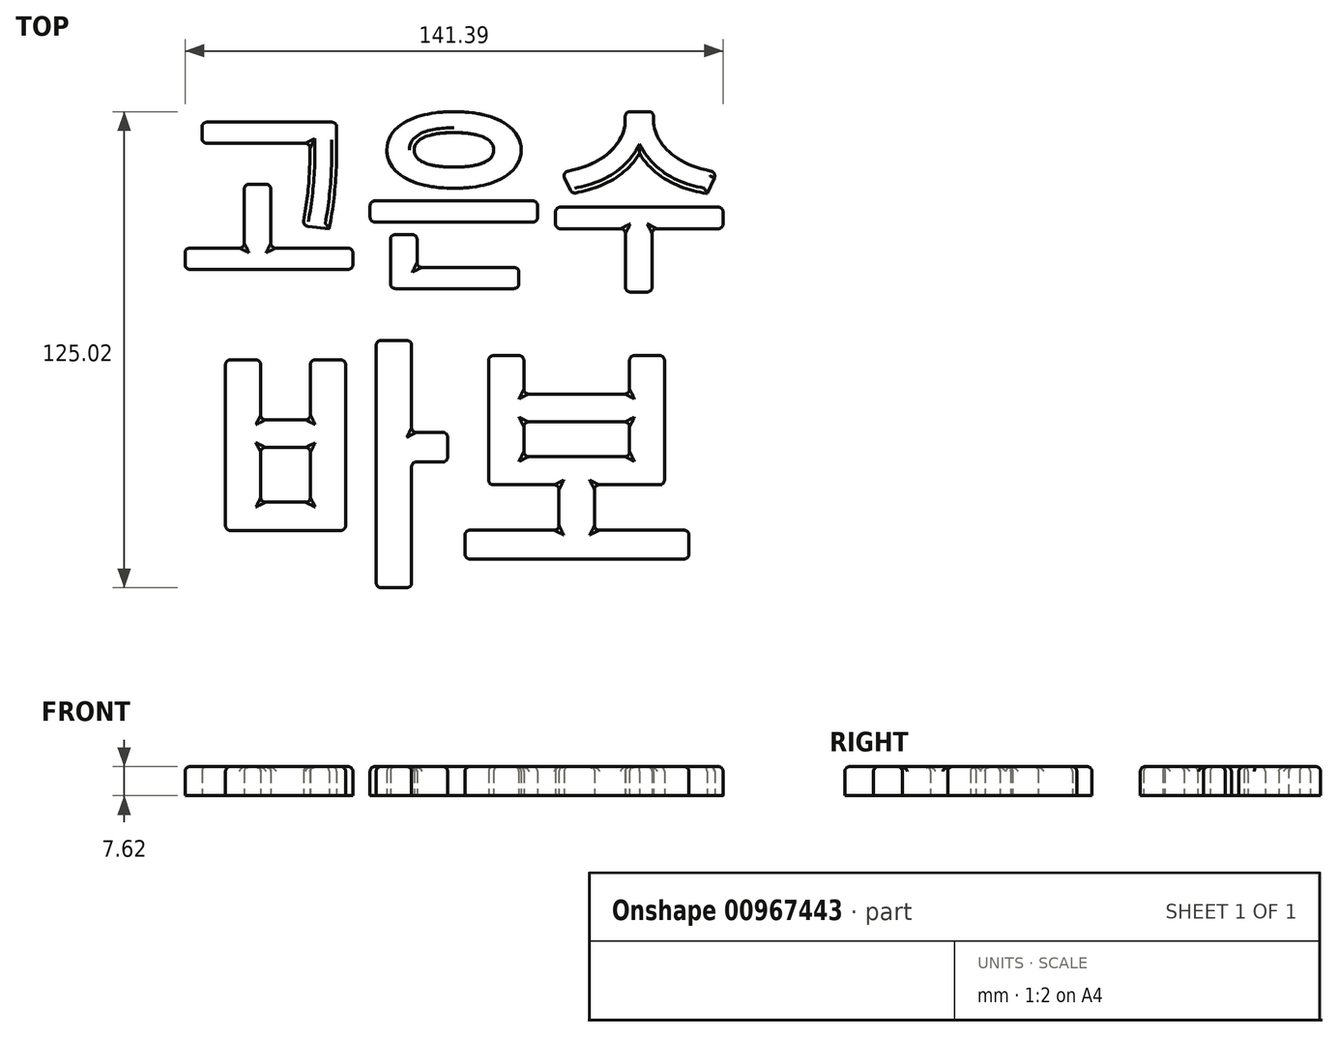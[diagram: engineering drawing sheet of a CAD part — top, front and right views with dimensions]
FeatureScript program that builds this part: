
annotation { "Feature Type Name" : "Feature", "Feature Type Description" : "" }
export const myFeature = defineFeature(function(context is Context, id is Id, definition is map)
    precondition{}
    {
        {
            var Q0;
            Q0=qCreatedBy(makeId("Top.planeOp"),FACE);
            var sketch = newSketch(context, id + "F0", { "sketchPlane" : qUnion([Q0])});
            skText(sketch, "E0", { "text": "고은수", "fontName": "NotoSansCJKkr-Bold.otf"});
            skText(sketch, "E1", { "text": "바보", "fontName": "NotoSansCJKkr-Bold.otf"});
            skLineSegment(sketch, "E2", {"start": v(0, 12.7) * mm, "end": v(0, -12.7) * mm, "construction": true});
            skLineSegment(sketch, "E3", {"start": v(-73.36, 50.8) * mm, "end": v(-73.36, -63.5) * mm, "construction": true});
            const initialGuessF0  = {"E0": [-0.07336, 0.0127, 1, 0, 0.0381], "E1": [-0.0654, -0.0635, 1, 0, 0.0508]};
            skSetInitialGuess(sketch, initialGuessF0);
            skSolve(sketch);
        }
        {
            var Q0;
            Q0 = qSketchRegion(id + "F0", true);
            extrude(context, id + "F1", {"entities" : qUnion([Q0]), "depth" : 7.62 * mm, "offsetDistance" : 25.4 * mm});
        }
        {
            var Q0;
            Q0=makeQuery(id+"F1.opExtrude","CAP_EDGE",EDGE,{"disambiguationData":[OSD([sQuery(id+"F0.wireOp",EDGE,"E0.sketch_text.stroke-4")])],"isStart":false});
            var Q1;
            Q1=makeQuery(id+"F1.opExtrude","CAP_EDGE",EDGE,{"disambiguationData":[OSD([sQuery(id+"F0.wireOp",EDGE,"E0.sketch_text.stroke-3")])],"isStart":false});
            var Q2;
            Q2=makeQuery(id+"F1.opExtrude","CAP_EDGE",EDGE,{"disambiguationData":[OSD([sQuery(id+"F0.wireOp",EDGE,"E0.sketch_text.stroke-2")])],"isStart":false});
            var Q3;
            Q3=makeQuery(id+"F1.opExtrude","CAP_EDGE",EDGE,{"disambiguationData":[OSD([sQuery(id+"F0.wireOp",EDGE,"E0.sketch_text.stroke-0")])],"isStart":false});
            var Q4;
            Q4=makeQuery(id+"F1.opExtrude","CAP_EDGE",EDGE,{"disambiguationData":[OSD([sQuery(id+"F0.wireOp",EDGE,"E0.sketch_text.stroke-5")])],"isStart":false});
            var Q5;
            Q5=makeQuery(id+"F1.opExtrude","CAP_EDGE",EDGE,{"disambiguationData":[OSD([sQuery(id+"F0.wireOp",EDGE,"E0.sketch_text.stroke-6")])],"isStart":false});
            var Q6;
            Q6=makeQuery(id+"F1.opExtrude","CAP_EDGE",EDGE,{"disambiguationData":[OSD([sQuery(id+"F0.wireOp",EDGE,"E0.sketch_text.stroke-7")])],"isStart":false});
            var Q7;
            Q7=makeQuery(id+"F1.opExtrude","CAP_EDGE",EDGE,{"disambiguationData":[OSD([sQuery(id+"F0.wireOp",EDGE,"E0.sketch_text.stroke-8")])],"isStart":false});
            var Q8;
            Q8=makeQuery(id+"F1.opExtrude","CAP_EDGE",EDGE,{"disambiguationData":[OSD([sQuery(id+"F0.wireOp",EDGE,"E0.sketch_text.stroke-10")])],"isStart":false});
            var Q9;
            Q9=makeQuery(id+"F1.opExtrude","CAP_EDGE",EDGE,{"disambiguationData":[OSD([sQuery(id+"F0.wireOp",EDGE,"E0.sketch_text.stroke-11")])],"isStart":false});
            var Q10;
            Q10=makeQuery(id+"F1.opExtrude","CAP_EDGE",EDGE,{"disambiguationData":[OSD([sQuery(id+"F0.wireOp",EDGE,"E0.sketch_text.stroke-12")])],"isStart":false});
            var Q11;
            Q11=makeQuery(id+"F1.opExtrude","CAP_EDGE",EDGE,{"disambiguationData":[OSD([sQuery(id+"F0.wireOp",EDGE,"E0.sketch_text.stroke-14")])],"isStart":false});
            var Q12;
            Q12=makeQuery(id+"F1.opExtrude","CAP_EDGE",EDGE,{"disambiguationData":[OSD([sQuery(id+"F0.wireOp",EDGE,"E0.sketch_text.stroke-13")])],"isStart":false});
            var Q13;
            Q13=makeQuery(id+"F1.opExtrude","CAP_EDGE",EDGE,{"disambiguationData":[OSD([sQuery(id+"F0.wireOp",EDGE,"E0.sketch_text.stroke-29")])],"isStart":false});
            var Q14;
            Q14=makeQuery(id+"F1.opExtrude","CAP_EDGE",EDGE,{"disambiguationData":[OSD([sQuery(id+"F0.wireOp",EDGE,"E0.sketch_text.stroke-32")])],"isStart":false});
            var Q15;
            Q15=makeQuery(id+"F1.opExtrude","CAP_EDGE",EDGE,{"disambiguationData":[OSD([sQuery(id+"F0.wireOp",EDGE,"E0.sketch_text.stroke-9")])],"isStart":false});
            var Q16;
            Q16=makeQuery(id+"F1.opExtrude","CAP_EDGE",EDGE,{"disambiguationData":[OSD([sQuery(id+"F0.wireOp",EDGE,"E0.sketch_text.stroke-30")])],"isStart":false});
            var Q17;
            Q17=makeQuery(id+"F1.opExtrude","CAP_EDGE",EDGE,{"disambiguationData":[OSD([sQuery(id+"F0.wireOp",EDGE,"E0.sketch_text.stroke-31")])],"isStart":false});
            var Q18;
            Q18=makeQuery(id+"F1.opExtrude","CAP_EDGE",EDGE,{"disambiguationData":[OSD([sQuery(id+"F0.wireOp",EDGE,"E0.sketch_text.stroke-19")])],"isStart":false});
            var Q19;
            Q19=makeQuery(id+"F1.opExtrude","CAP_EDGE",EDGE,{"disambiguationData":[OSD([sQuery(id+"F0.wireOp",EDGE,"E0.sketch_text.stroke-16")])],"isStart":false});
            var Q20;
            Q20=makeQuery(id+"F1.opExtrude","CAP_EDGE",EDGE,{"disambiguationData":[OSD([sQuery(id+"F0.wireOp",EDGE,"E0.sketch_text.stroke-27")])],"isStart":false});
            var Q21;
            Q21=makeQuery(id+"F1.opExtrude","CAP_EDGE",EDGE,{"disambiguationData":[OSD([sQuery(id+"F0.wireOp",EDGE,"E0.sketch_text.stroke-28")])],"isStart":false});
            var Q22;
            Q22=makeQuery(id+"F1.opExtrude","CAP_EDGE",EDGE,{"disambiguationData":[OSD([sQuery(id+"F0.wireOp",EDGE,"E0.sketch_text.stroke-23")])],"isStart":false});
            var Q23;
            Q23=makeQuery(id+"F1.opExtrude","CAP_EDGE",EDGE,{"disambiguationData":[OSD([sQuery(id+"F0.wireOp",EDGE,"E0.sketch_text.stroke-24")])],"isStart":false});
            var Q24;
            Q24=makeQuery(id+"F1.opExtrude","CAP_EDGE",EDGE,{"disambiguationData":[OSD([sQuery(id+"F0.wireOp",EDGE,"E0.sketch_text.stroke-25")])],"isStart":false});
            var Q25;
            Q25=makeQuery(id+"F1.opExtrude","CAP_EDGE",EDGE,{"disambiguationData":[OSD([sQuery(id+"F0.wireOp",EDGE,"E0.sketch_text.stroke-26")])],"isStart":false});
            var Q26;
            Q26=makeQuery(id+"F1.opExtrude","CAP_EDGE",EDGE,{"disambiguationData":[OSD([sQuery(id+"F0.wireOp",EDGE,"E0.sketch_text.stroke-43")])],"isStart":false});
            var Q27;
            Q27=makeQuery(id+"F1.opExtrude","CAP_EDGE",EDGE,{"disambiguationData":[OSD([sQuery(id+"F0.wireOp",EDGE,"E0.sketch_text.stroke-44")])],"isStart":false});
            var Q28;
            Q28=makeQuery(id+"F1.opExtrude","CAP_EDGE",EDGE,{"disambiguationData":[OSD([sQuery(id+"F0.wireOp",EDGE,"E0.sketch_text.stroke-45")])],"isStart":false});
            var Q29;
            Q29=makeQuery(id+"F1.opExtrude","CAP_EDGE",EDGE,{"disambiguationData":[OSD([sQuery(id+"F0.wireOp",EDGE,"E0.sketch_text.stroke-47")])],"isStart":false});
            var Q30;
            Q30=makeQuery(id+"F1.opExtrude","CAP_EDGE",EDGE,{"disambiguationData":[OSD([sQuery(id+"F0.wireOp",EDGE,"E0.sketch_text.stroke-48")])],"isStart":false});
            var Q31;
            Q31=makeQuery(id+"F1.opExtrude","CAP_EDGE",EDGE,{"disambiguationData":[OSD([sQuery(id+"F0.wireOp",EDGE,"E0.sketch_text.stroke-42")])],"isStart":false});
            var Q32;
            Q32=makeQuery(id+"F1.opExtrude","CAP_EDGE",EDGE,{"disambiguationData":[OSD([sQuery(id+"F0.wireOp",EDGE,"E0.sketch_text.stroke-46")])],"isStart":false});
            var Q33;
            Q33=makeQuery(id+"F1.opExtrude","CAP_EDGE",EDGE,{"disambiguationData":[OSD([sQuery(id+"F0.wireOp",EDGE,"E0.sketch_text.stroke-40")])],"isStart":false});
            var Q34;
            Q34=makeQuery(id+"F1.opExtrude","CAP_EDGE",EDGE,{"disambiguationData":[OSD([sQuery(id+"F0.wireOp",EDGE,"E0.sketch_text.stroke-39")])],"isStart":false});
            var Q35;
            Q35=makeQuery(id+"F1.opExtrude","CAP_FACE",FACE,{"disambiguationData":[OSD([sQuery(id+"F0.wireOp",EDGE,"E0.sketch_text.stroke-33"),sQuery(id+"F0.wireOp",EDGE,"E0.sketch_text.stroke-34"),sQuery(id+"F0.wireOp",EDGE,"E0.sketch_text.stroke-35"),sQuery(id+"F0.wireOp",EDGE,"E0.sketch_text.stroke-36"),sQuery(id+"F0.wireOp",EDGE,"E0.sketch_text.stroke-37"),sQuery(id+"F0.wireOp",EDGE,"E0.sketch_text.stroke-38"),sQuery(id+"F0.wireOp",EDGE,"E0.sketch_text.stroke-39"),sQuery(id+"F0.wireOp",EDGE,"E0.sketch_text.stroke-40"),sQuery(id+"F0.wireOp",EDGE,"E0.sketch_text.stroke-41")])],"isStart":false});
            var Q36;
            Q36=makeQuery(id+"F1.opExtrude","CAP_EDGE",EDGE,{"disambiguationData":[OSD([sQuery(id+"F0.wireOp",EDGE,"E1.sketch_text.stroke-28")])],"isStart":false});
            var Q37;
            Q37=makeQuery(id+"F1.opExtrude","CAP_EDGE",EDGE,{"disambiguationData":[OSD([sQuery(id+"F0.wireOp",EDGE,"E1.sketch_text.stroke-26")])],"isStart":false});
            var Q38;
            Q38=makeQuery(id+"F1.opExtrude","CAP_FACE",FACE,{"disambiguationData":[OSD([sQuery(id+"F0.wireOp",EDGE,"E1.sketch_text.stroke-20"),sQuery(id+"F0.wireOp",EDGE,"E1.sketch_text.stroke-21"),sQuery(id+"F0.wireOp",EDGE,"E1.sketch_text.stroke-22"),sQuery(id+"F0.wireOp",EDGE,"E1.sketch_text.stroke-23"),sQuery(id+"F0.wireOp",EDGE,"E1.sketch_text.stroke-24"),sQuery(id+"F0.wireOp",EDGE,"E1.sketch_text.stroke-25"),sQuery(id+"F0.wireOp",EDGE,"E1.sketch_text.stroke-26"),sQuery(id+"F0.wireOp",EDGE,"E1.sketch_text.stroke-27"),sQuery(id+"F0.wireOp",EDGE,"E1.sketch_text.stroke-28"),sQuery(id+"F0.wireOp",EDGE,"E1.sketch_text.stroke-29"),sQuery(id+"F0.wireOp",EDGE,"E1.sketch_text.stroke-30"),sQuery(id+"F0.wireOp",EDGE,"E1.sketch_text.stroke-31"),sQuery(id+"F0.wireOp",EDGE,"E1.sketch_text.stroke-32"),sQuery(id+"F0.wireOp",EDGE,"E1.sketch_text.stroke-33"),sQuery(id+"F0.wireOp",EDGE,"E1.sketch_text.stroke-34"),sQuery(id+"F0.wireOp",EDGE,"E1.sketch_text.stroke-35"),sQuery(id+"F0.wireOp",EDGE,"E1.sketch_text.stroke-36"),sQuery(id+"F0.wireOp",EDGE,"E1.sketch_text.stroke-37"),sQuery(id+"F0.wireOp",EDGE,"E1.sketch_text.stroke-38"),sQuery(id+"F0.wireOp",EDGE,"E1.sketch_text.stroke-39")])],"isStart":false});
            var Q39;
            Q39=makeQuery(id+"F1.opExtrude","CAP_FACE",FACE,{"disambiguationData":[OSD([sQuery(id+"F0.wireOp",EDGE,"E1.sketch_text.stroke-12"),sQuery(id+"F0.wireOp",EDGE,"E1.sketch_text.stroke-13"),sQuery(id+"F0.wireOp",EDGE,"E1.sketch_text.stroke-14"),sQuery(id+"F0.wireOp",EDGE,"E1.sketch_text.stroke-15"),sQuery(id+"F0.wireOp",EDGE,"E1.sketch_text.stroke-16"),sQuery(id+"F0.wireOp",EDGE,"E1.sketch_text.stroke-17"),sQuery(id+"F0.wireOp",EDGE,"E1.sketch_text.stroke-18"),sQuery(id+"F0.wireOp",EDGE,"E1.sketch_text.stroke-19")])],"isStart":false});
            var Q40;
            Q40=makeQuery(id+"F1.opExtrude","CAP_FACE",FACE,{"disambiguationData":[OSD([sQuery(id+"F0.wireOp",EDGE,"E1.sketch_text.stroke-0"),sQuery(id+"F0.wireOp",EDGE,"E1.sketch_text.stroke-1"),sQuery(id+"F0.wireOp",EDGE,"E1.sketch_text.stroke-2"),sQuery(id+"F0.wireOp",EDGE,"E1.sketch_text.stroke-3"),sQuery(id+"F0.wireOp",EDGE,"E1.sketch_text.stroke-4"),sQuery(id+"F0.wireOp",EDGE,"E1.sketch_text.stroke-5"),sQuery(id+"F0.wireOp",EDGE,"E1.sketch_text.stroke-6"),sQuery(id+"F0.wireOp",EDGE,"E1.sketch_text.stroke-7"),sQuery(id+"F0.wireOp",EDGE,"E1.sketch_text.stroke-8"),sQuery(id+"F0.wireOp",EDGE,"E1.sketch_text.stroke-9"),sQuery(id+"F0.wireOp",EDGE,"E1.sketch_text.stroke-10"),sQuery(id+"F0.wireOp",EDGE,"E1.sketch_text.stroke-11")])],"isStart":false});
            var Q41;
            Q41=makeQuery(id+"F1.opExtrude","CAP_EDGE",EDGE,{"disambiguationData":[OSD([sQuery(id+"F0.wireOp",EDGE,"E0.sketch_text.stroke-22")])],"isStart":false});
            var Q42;
            Q42=makeQuery(id+"F1.opExtrude","SWEPT_EDGE",EDGE,{"disambiguationData":[OSD([sQuery(id+"F0.wireOp",EDGE,"E1.sketch_text.stroke-16"),sQuery(id+"F0.wireOp",EDGE,"E1.sketch_text.stroke-17")])]});
            var Q43;
            Q43=makeQuery(id+"F1.opExtrude","SWEPT_EDGE",EDGE,{"disambiguationData":[OSD([sQuery(id+"F0.wireOp",EDGE,"E1.sketch_text.stroke-17"),sQuery(id+"F0.wireOp",EDGE,"E1.sketch_text.stroke-18")])]});
            var Q44;
            Q44=makeQuery(id+"F1.opExtrude","SWEPT_EDGE",EDGE,{"disambiguationData":[OSD([sQuery(id+"F0.wireOp",EDGE,"E1.sketch_text.stroke-18"),sQuery(id+"F0.wireOp",EDGE,"E1.sketch_text.stroke-19")])]});
            var Q45;
            Q45=makeQuery(id+"F1.opExtrude","SWEPT_EDGE",EDGE,{"disambiguationData":[OSD([sQuery(id+"F0.wireOp",EDGE,"E1.sketch_text.stroke-12"),sQuery(id+"F0.wireOp",EDGE,"E1.sketch_text.stroke-19")])]});
            var Q46;
            Q46=makeQuery(id+"F1.opExtrude","SWEPT_EDGE",EDGE,{"disambiguationData":[OSD([sQuery(id+"F0.wireOp",EDGE,"E1.sketch_text.stroke-13"),sQuery(id+"F0.wireOp",EDGE,"E1.sketch_text.stroke-14")])]});
            var Q47;
            Q47=makeQuery(id+"F1.opExtrude","SWEPT_EDGE",EDGE,{"disambiguationData":[OSD([sQuery(id+"F0.wireOp",EDGE,"E1.sketch_text.stroke-8"),sQuery(id+"F0.wireOp",EDGE,"E1.sketch_text.stroke-9")])]});
            var Q48;
            Q48=makeQuery(id+"F1.opExtrude","SWEPT_EDGE",EDGE,{"disambiguationData":[OSD([sQuery(id+"F0.wireOp",EDGE,"E1.sketch_text.stroke-9"),sQuery(id+"F0.wireOp",EDGE,"E1.sketch_text.stroke-10")])]});
            var Q49;
            Q49=makeQuery(id+"F1.opExtrude","SWEPT_EDGE",EDGE,{"disambiguationData":[OSD([sQuery(id+"F0.wireOp",EDGE,"E1.sketch_text.stroke-5"),sQuery(id+"F0.wireOp",EDGE,"E1.sketch_text.stroke-6")])]});
            var Q50;
            Q50=makeQuery(id+"F1.opExtrude","SWEPT_EDGE",EDGE,{"disambiguationData":[OSD([sQuery(id+"F0.wireOp",EDGE,"E1.sketch_text.stroke-7"),sQuery(id+"F0.wireOp",EDGE,"E1.sketch_text.stroke-8")])]});
            var Q51;
            Q51=makeQuery(id+"F1.opExtrude","SWEPT_EDGE",EDGE,{"disambiguationData":[OSD([sQuery(id+"F0.wireOp",EDGE,"E1.sketch_text.stroke-36"),sQuery(id+"F0.wireOp",EDGE,"E1.sketch_text.stroke-37")])]});
            fillet(context, id + "F2", {"entities" : qUnion([Q0, Q1, Q2, Q3, Q4, Q5, Q6, Q7, Q8, Q9, Q10, Q11, Q12, Q13, Q14, Q15, Q16, Q17, Q18, Q19, Q20, Q21, Q22, Q23, Q24, Q25, Q26, Q27, Q28, Q29, Q30, Q31, Q32, Q33, Q34, Q35, Q36, Q37, Q38, Q39, Q40, Q41, Q42, Q43, Q44, Q45, Q46, Q47, Q48, Q49, Q50, Q51]), "radius" : 1.27 * mm, "tangentPropagation" : true, "allowEdgeOverflow" : false});
        }
        {
            var Q0;
            Q0=makeQuery(id+"F1.opExtrude","SWEPT_EDGE",EDGE,{"disambiguationData":[OSD([sQuery(id+"F0.wireOp",EDGE,"E1.sketch_text.stroke-1"),sQuery(id+"F0.wireOp",EDGE,"E1.sketch_text.stroke-2")])]});
            var Q1;
            Q1=makeQuery(id+"F1.opExtrude","SWEPT_EDGE",EDGE,{"disambiguationData":[OSD([sQuery(id+"F0.wireOp",EDGE,"E0.sketch_text.stroke-11"),sQuery(id+"F0.wireOp",EDGE,"E0.sketch_text.stroke-12")])]});
            var Q2;
            Q2=makeQuery(id+"F1.opExtrude","SWEPT_EDGE",EDGE,{"disambiguationData":[OSD([sQuery(id+"F0.wireOp",EDGE,"E0.sketch_text.stroke-12"),sQuery(id+"F0.wireOp",EDGE,"E0.sketch_text.stroke-13")])]});
            var Q3;
            Q3=makeQuery(id+"F1.opExtrude","SWEPT_EDGE",EDGE,{"disambiguationData":[OSD([sQuery(id+"F0.wireOp",EDGE,"E0.sketch_text.stroke-7"),sQuery(id+"F0.wireOp",EDGE,"E0.sketch_text.stroke-8")])]});
            var Q4;
            Q4=makeQuery(id+"F1.opExtrude","SWEPT_EDGE",EDGE,{"disambiguationData":[OSD([sQuery(id+"F0.wireOp",EDGE,"E0.sketch_text.stroke-8"),sQuery(id+"F0.wireOp",EDGE,"E0.sketch_text.stroke-9")])]});
            var Q5;
            Q5=makeQuery(id+"F1.opExtrude","SWEPT_EDGE",EDGE,{"disambiguationData":[OSD([sQuery(id+"F0.wireOp",EDGE,"E0.sketch_text.stroke-3"),sQuery(id+"F0.wireOp",EDGE,"E0.sketch_text.stroke-4")])]});
            var Q6;
            Q6=makeQuery(id+"F1.opExtrude","SWEPT_EDGE",EDGE,{"disambiguationData":[OSD([sQuery(id+"F0.wireOp",EDGE,"E0.sketch_text.stroke-2"),sQuery(id+"F0.wireOp",EDGE,"E0.sketch_text.stroke-3")])]});
            var Q7;
            Q7=makeQuery(id+"F1.opExtrude","SWEPT_EDGE",EDGE,{"disambiguationData":[OSD([sQuery(id+"F0.wireOp",EDGE,"E0.sketch_text.stroke-4"),sQuery(id+"F0.wireOp",EDGE,"E0.sketch_text.stroke-5")])]});
            var Q8;
            Q8=makeQuery(id+"F1.opExtrude","SWEPT_EDGE",EDGE,{"disambiguationData":[OSD([sQuery(id+"F0.wireOp",EDGE,"E0.sketch_text.stroke-5"),sQuery(id+"F0.wireOp",EDGE,"E0.sketch_text.stroke-6")])]});
            var Q9;
            Q9=makeQuery(id+"F1.opExtrude","SWEPT_EDGE",EDGE,{"disambiguationData":[OSD([sQuery(id+"F0.wireOp",EDGE,"E0.sketch_text.stroke-9"),sQuery(id+"F0.wireOp",EDGE,"E0.sketch_text.stroke-10")])]});
            var Q10;
            Q10=makeQuery(id+"F1.opExtrude","SWEPT_EDGE",EDGE,{"disambiguationData":[OSD([sQuery(id+"F0.wireOp",EDGE,"E1.sketch_text.stroke-4"),sQuery(id+"F0.wireOp",EDGE,"E1.sketch_text.stroke-11")])]});
            var Q11;
            Q11=makeQuery(id+"F1.opExtrude","SWEPT_EDGE",EDGE,{"disambiguationData":[OSD([sQuery(id+"F0.wireOp",EDGE,"E1.sketch_text.stroke-6"),sQuery(id+"F0.wireOp",EDGE,"E1.sketch_text.stroke-7")])]});
            var Q12;
            Q12=makeQuery(id+"F1.opExtrude","SWEPT_EDGE",EDGE,{"disambiguationData":[OSD([sQuery(id+"F0.wireOp",EDGE,"E1.sketch_text.stroke-10"),sQuery(id+"F0.wireOp",EDGE,"E1.sketch_text.stroke-11")])]});
            var Q13;
            {var subQ0=sQuery(id+"F0.wireOp",EDGE,"E1.sketch_text.stroke-7");Q13=makeQuery(id+"F2.opFillet","BLEND_EDGE",EDGE,{"blendedFrom":[makeQuery(id+"F1.opExtrude","SWEPT_EDGE",EDGE,{"disambiguationData":[OSD([subQ0,sQuery(id+"F0.wireOp",EDGE,"E1.sketch_text.stroke-8")])]}),makeQuery(id+"F1.opExtrude","SWEPT_FACE",FACE,{"disambiguationData":[OSD([subQ0])]})],"blendedInto":[makeQuery(id+"F1.opExtrude","SWEPT_FACE",FACE,{"disambiguationData":[OSD([subQ0])]})]});}
            var Q14;
            Q14=makeQuery(id+"F1.opExtrude","SWEPT_EDGE",EDGE,{"disambiguationData":[OSD([sQuery(id+"F0.wireOp",EDGE,"E1.sketch_text.stroke-0"),sQuery(id+"F0.wireOp",EDGE,"E1.sketch_text.stroke-3")])]});
            var Q15;
            Q15=makeQuery(id+"F1.opExtrude","SWEPT_EDGE",EDGE,{"disambiguationData":[OSD([sQuery(id+"F0.wireOp",EDGE,"E1.sketch_text.stroke-14"),sQuery(id+"F0.wireOp",EDGE,"E1.sketch_text.stroke-15")])]});
            var Q16;
            Q16=makeQuery(id+"F1.opExtrude","SWEPT_EDGE",EDGE,{"disambiguationData":[OSD([sQuery(id+"F0.wireOp",EDGE,"E1.sketch_text.stroke-15"),sQuery(id+"F0.wireOp",EDGE,"E1.sketch_text.stroke-16")])]});
            var Q17;
            Q17=makeQuery(id+"F1.opExtrude","SWEPT_EDGE",EDGE,{"disambiguationData":[OSD([sQuery(id+"F0.wireOp",EDGE,"E1.sketch_text.stroke-31"),sQuery(id+"F0.wireOp",EDGE,"E1.sketch_text.stroke-32")])]});
            var Q18;
            Q18=makeQuery(id+"F1.opExtrude","SWEPT_EDGE",EDGE,{"disambiguationData":[OSD([sQuery(id+"F0.wireOp",EDGE,"E1.sketch_text.stroke-32"),sQuery(id+"F0.wireOp",EDGE,"E1.sketch_text.stroke-33")])]});
            var Q19;
            Q19=makeQuery(id+"F1.opExtrude","SWEPT_EDGE",EDGE,{"disambiguationData":[OSD([sQuery(id+"F0.wireOp",EDGE,"E1.sketch_text.stroke-30"),sQuery(id+"F0.wireOp",EDGE,"E1.sketch_text.stroke-31")])]});
            var Q20;
            Q20=makeQuery(id+"F1.opExtrude","SWEPT_EDGE",EDGE,{"disambiguationData":[OSD([sQuery(id+"F0.wireOp",EDGE,"E1.sketch_text.stroke-21"),sQuery(id+"F0.wireOp",EDGE,"E1.sketch_text.stroke-22")])]});
            var Q21;
            Q21=makeQuery(id+"F1.opExtrude","SWEPT_EDGE",EDGE,{"disambiguationData":[OSD([sQuery(id+"F0.wireOp",EDGE,"E1.sketch_text.stroke-28"),sQuery(id+"F0.wireOp",EDGE,"E1.sketch_text.stroke-29")])]});
            var Q22;
            Q22=makeQuery(id+"F1.opExtrude","SWEPT_EDGE",EDGE,{"disambiguationData":[OSD([sQuery(id+"F0.wireOp",EDGE,"E1.sketch_text.stroke-27"),sQuery(id+"F0.wireOp",EDGE,"E1.sketch_text.stroke-28")])]});
            var Q23;
            Q23=makeQuery(id+"F1.opExtrude","SWEPT_EDGE",EDGE,{"disambiguationData":[OSD([sQuery(id+"F0.wireOp",EDGE,"E1.sketch_text.stroke-38"),sQuery(id+"F0.wireOp",EDGE,"E1.sketch_text.stroke-39")])]});
            var Q24;
            Q24=makeQuery(id+"F1.opExtrude","SWEPT_EDGE",EDGE,{"disambiguationData":[OSD([sQuery(id+"F0.wireOp",EDGE,"E1.sketch_text.stroke-34"),sQuery(id+"F0.wireOp",EDGE,"E1.sketch_text.stroke-35")])]});
            var Q25;
            Q25=makeQuery(id+"F1.opExtrude","SWEPT_EDGE",EDGE,{"disambiguationData":[OSD([sQuery(id+"F0.wireOp",EDGE,"E0.sketch_text.stroke-24"),sQuery(id+"F0.wireOp",EDGE,"E0.sketch_text.stroke-25")])]});
            var Q26;
            Q26=makeQuery(id+"F1.opExtrude","SWEPT_EDGE",EDGE,{"disambiguationData":[OSD([sQuery(id+"F0.wireOp",EDGE,"E0.sketch_text.stroke-23"),sQuery(id+"F0.wireOp",EDGE,"E0.sketch_text.stroke-24")])]});
            var Q27;
            Q27=makeQuery(id+"F1.opExtrude","SWEPT_EDGE",EDGE,{"disambiguationData":[OSD([sQuery(id+"F0.wireOp",EDGE,"E0.sketch_text.stroke-29"),sQuery(id+"F0.wireOp",EDGE,"E0.sketch_text.stroke-32")])]});
            var Q28;
            Q28=makeQuery(id+"F1.opExtrude","SWEPT_EDGE",EDGE,{"disambiguationData":[OSD([sQuery(id+"F0.wireOp",EDGE,"E0.sketch_text.stroke-29"),sQuery(id+"F0.wireOp",EDGE,"E0.sketch_text.stroke-30")])]});
            var Q29;
            Q29=makeQuery(id+"F1.opExtrude","SWEPT_EDGE",EDGE,{"disambiguationData":[OSD([sQuery(id+"F0.wireOp",EDGE,"E0.sketch_text.stroke-31"),sQuery(id+"F0.wireOp",EDGE,"E0.sketch_text.stroke-32")])]});
            var Q30;
            Q30=makeQuery(id+"F1.opExtrude","SWEPT_EDGE",EDGE,{"disambiguationData":[OSD([sQuery(id+"F0.wireOp",EDGE,"E0.sketch_text.stroke-38"),sQuery(id+"F0.wireOp",EDGE,"E0.sketch_text.stroke-39")])]});
            var Q31;
            Q31=makeQuery(id+"F1.opExtrude","SWEPT_EDGE",EDGE,{"disambiguationData":[OSD([sQuery(id+"F0.wireOp",EDGE,"E0.sketch_text.stroke-42"),sQuery(id+"F0.wireOp",EDGE,"E0.sketch_text.stroke-43")])]});
            var Q32;
            Q32=makeQuery(id+"F1.opExtrude","SWEPT_EDGE",EDGE,{"disambiguationData":[OSD([sQuery(id+"F0.wireOp",EDGE,"E0.sketch_text.stroke-43"),sQuery(id+"F0.wireOp",EDGE,"E0.sketch_text.stroke-44")])]});
            var Q33;
            Q33=makeQuery(id+"F1.opExtrude","SWEPT_EDGE",EDGE,{"disambiguationData":[OSD([sQuery(id+"F0.wireOp",EDGE,"E0.sketch_text.stroke-37"),sQuery(id+"F0.wireOp",EDGE,"E0.sketch_text.stroke-38")])]});
            var Q34;
            Q34=makeQuery(id+"F1.opExtrude","SWEPT_EDGE",EDGE,{"disambiguationData":[OSD([sQuery(id+"F0.wireOp",EDGE,"E0.sketch_text.stroke-35"),sQuery(id+"F0.wireOp",EDGE,"E0.sketch_text.stroke-36")])]});
            var Q35;
            Q35=makeQuery(id+"F1.opExtrude","SWEPT_EDGE",EDGE,{"disambiguationData":[OSD([sQuery(id+"F0.wireOp",EDGE,"E0.sketch_text.stroke-34"),sQuery(id+"F0.wireOp",EDGE,"E0.sketch_text.stroke-35")])]});
            var Q36;
            Q36=makeQuery(id+"F1.opExtrude","SWEPT_EDGE",EDGE,{"disambiguationData":[OSD([sQuery(id+"F0.wireOp",EDGE,"E0.sketch_text.stroke-33"),sQuery(id+"F0.wireOp",EDGE,"E0.sketch_text.stroke-41")])]});
            var Q37;
            Q37=makeQuery(id+"F1.opExtrude","SWEPT_EDGE",EDGE,{"disambiguationData":[OSD([sQuery(id+"F0.wireOp",EDGE,"E0.sketch_text.stroke-45"),sQuery(id+"F0.wireOp",EDGE,"E0.sketch_text.stroke-46")])]});
            var Q38;
            Q38=makeQuery(id+"F1.opExtrude","SWEPT_EDGE",EDGE,{"disambiguationData":[OSD([sQuery(id+"F0.wireOp",EDGE,"E1.sketch_text.stroke-26"),sQuery(id+"F0.wireOp",EDGE,"E1.sketch_text.stroke-27")])]});
            var Q39;
            Q39=makeQuery(id+"F1.opExtrude","SWEPT_EDGE",EDGE,{"disambiguationData":[OSD([sQuery(id+"F0.wireOp",EDGE,"E0.sketch_text.stroke-48"),sQuery(id+"F0.wireOp",EDGE,"E0.sketch_text.stroke-49")])]});
            var Q40;
            Q40=makeQuery(id+"F1.opExtrude","SWEPT_EDGE",EDGE,{"disambiguationData":[OSD([sQuery(id+"F0.wireOp",EDGE,"E0.sketch_text.stroke-46"),sQuery(id+"F0.wireOp",EDGE,"E0.sketch_text.stroke-47")])]});
            var Q41;
            Q41=makeQuery(id+"F1.opExtrude","SWEPT_EDGE",EDGE,{"disambiguationData":[OSD([sQuery(id+"F0.wireOp",EDGE,"E0.sketch_text.stroke-25"),sQuery(id+"F0.wireOp",EDGE,"E0.sketch_text.stroke-26")])]});
            var Q42;
            Q42=makeQuery(id+"F1.opExtrude","SWEPT_EDGE",EDGE,{"disambiguationData":[OSD([sQuery(id+"F0.wireOp",EDGE,"E0.sketch_text.stroke-27"),sQuery(id+"F0.wireOp",EDGE,"E0.sketch_text.stroke-28")])]});
            var Q43;
            Q43=makeQuery(id+"F1.opExtrude","SWEPT_EDGE",EDGE,{"disambiguationData":[OSD([sQuery(id+"F0.wireOp",EDGE,"E0.sketch_text.stroke-23"),sQuery(id+"F0.wireOp",EDGE,"E0.sketch_text.stroke-28")])]});
            var Q44;
            Q44=makeQuery(id+"F1.opExtrude","SWEPT_EDGE",EDGE,{"disambiguationData":[OSD([sQuery(id+"F0.wireOp",EDGE,"E1.sketch_text.stroke-29"),sQuery(id+"F0.wireOp",EDGE,"E1.sketch_text.stroke-30")])]});
            var Q45;
            Q45=makeQuery(id+"F1.opExtrude","SWEPT_EDGE",EDGE,{"disambiguationData":[OSD([sQuery(id+"F0.wireOp",EDGE,"E1.sketch_text.stroke-12"),sQuery(id+"F0.wireOp",EDGE,"E1.sketch_text.stroke-13")])]});
            var Q46;
            Q46=makeQuery(id+"F1.opExtrude","SWEPT_EDGE",EDGE,{"disambiguationData":[OSD([sQuery(id+"F0.wireOp",EDGE,"E1.sketch_text.stroke-22"),sQuery(id+"F0.wireOp",EDGE,"E1.sketch_text.stroke-23")])]});
            var Q47;
            Q47=makeQuery(id+"F1.opExtrude","SWEPT_EDGE",EDGE,{"disambiguationData":[OSD([sQuery(id+"F0.wireOp",EDGE,"E1.sketch_text.stroke-25"),sQuery(id+"F0.wireOp",EDGE,"E1.sketch_text.stroke-26")])]});
            var Q48;
            Q48=makeQuery(id+"F1.opExtrude","SWEPT_EDGE",EDGE,{"disambiguationData":[OSD([sQuery(id+"F0.wireOp",EDGE,"E1.sketch_text.stroke-24"),sQuery(id+"F0.wireOp",EDGE,"E1.sketch_text.stroke-39")])]});
            var Q49;
            Q49=makeQuery(id+"F1.opExtrude","SWEPT_EDGE",EDGE,{"disambiguationData":[OSD([sQuery(id+"F0.wireOp",EDGE,"E1.sketch_text.stroke-37"),sQuery(id+"F0.wireOp",EDGE,"E1.sketch_text.stroke-38")])]});
            var Q50;
            Q50=makeQuery(id+"F1.opExtrude","SWEPT_EDGE",EDGE,{"disambiguationData":[OSD([sQuery(id+"F0.wireOp",EDGE,"E0.sketch_text.stroke-26"),sQuery(id+"F0.wireOp",EDGE,"E0.sketch_text.stroke-27")])]});
            var Q51;
            Q51=makeQuery(id+"F1.opExtrude","SWEPT_EDGE",EDGE,{"disambiguationData":[OSD([sQuery(id+"F0.wireOp",EDGE,"E0.sketch_text.stroke-7"),sQuery(id+"F0.wireOp",EDGE,"E0.sketch_text.stroke-14")])]});
            var Q52;
            Q52=makeQuery(id+"F1.opExtrude","SWEPT_EDGE",EDGE,{"disambiguationData":[OSD([sQuery(id+"F0.wireOp",EDGE,"E0.sketch_text.stroke-1"),sQuery(id+"F0.wireOp",EDGE,"E0.sketch_text.stroke-2")])]});
            var Q53;
            Q53=makeQuery(id+"F1.opExtrude","SWEPT_EDGE",EDGE,{"disambiguationData":[OSD([sQuery(id+"F0.wireOp",EDGE,"E1.sketch_text.stroke-24"),sQuery(id+"F0.wireOp",EDGE,"E1.sketch_text.stroke-25")])]});
            var Q54;
            Q54=makeQuery(id+"F1.opExtrude","SWEPT_EDGE",EDGE,{"disambiguationData":[OSD([sQuery(id+"F0.wireOp",EDGE,"E0.sketch_text.stroke-47"),sQuery(id+"F0.wireOp",EDGE,"E0.sketch_text.stroke-48")])]});
            var Q55;
            Q55=makeQuery(id+"F1.opExtrude","SWEPT_EDGE",EDGE,{"disambiguationData":[OSD([sQuery(id+"F0.wireOp",EDGE,"E1.sketch_text.stroke-20"),sQuery(id+"F0.wireOp",EDGE,"E1.sketch_text.stroke-21")])]});
            var Q56;
            Q56=makeQuery(id+"F1.opExtrude","SWEPT_EDGE",EDGE,{"disambiguationData":[OSD([sQuery(id+"F0.wireOp",EDGE,"E0.sketch_text.stroke-44"),sQuery(id+"F0.wireOp",EDGE,"E0.sketch_text.stroke-45")])]});
            var Q57;
            Q57=makeQuery(id+"F2.opFillet","BLEND_EDGE",EDGE,{"blendedFrom":[makeQuery(id+"F1.opExtrude","CAP_EDGE",EDGE,{"disambiguationData":[OSD([sQuery(id+"F0.wireOp",EDGE,"E1.sketch_text.stroke-0")])],"isStart":false}),makeQuery(id+"F1.opExtrude","CAP_EDGE",EDGE,{"disambiguationData":[OSD([sQuery(id+"F0.wireOp",EDGE,"E1.sketch_text.stroke-1")])],"isStart":false})],"blendedInto":[]});
            var Q58;
            Q58=makeQuery(id+"F2.opFillet","BLEND_EDGE",EDGE,{"blendedFrom":[makeQuery(id+"F1.opExtrude","CAP_EDGE",EDGE,{"disambiguationData":[OSD([sQuery(id+"F0.wireOp",EDGE,"E1.sketch_text.stroke-2")])],"isStart":false}),makeQuery(id+"F1.opExtrude","CAP_EDGE",EDGE,{"disambiguationData":[OSD([sQuery(id+"F0.wireOp",EDGE,"E1.sketch_text.stroke-3")])],"isStart":false})],"blendedInto":[]});
            var Q59;
            Q59=makeQuery(id+"F2.opFillet","BLEND_EDGE",EDGE,{"blendedFrom":[makeQuery(id+"F1.opExtrude","CAP_EDGE",EDGE,{"disambiguationData":[OSD([sQuery(id+"F0.wireOp",EDGE,"E1.sketch_text.stroke-4")])],"isStart":false}),makeQuery(id+"F1.opExtrude","CAP_EDGE",EDGE,{"disambiguationData":[OSD([sQuery(id+"F0.wireOp",EDGE,"E1.sketch_text.stroke-5")])],"isStart":false})],"blendedInto":[]});
            var Q60;
            Q60=makeQuery(id+"F2.opFillet","BLEND_EDGE",EDGE,{"blendedFrom":[makeQuery(id+"F1.opExtrude","CAP_EDGE",EDGE,{"disambiguationData":[OSD([sQuery(id+"F0.wireOp",EDGE,"E1.sketch_text.stroke-20")])],"isStart":false}),makeQuery(id+"F1.opExtrude","CAP_EDGE",EDGE,{"disambiguationData":[OSD([sQuery(id+"F0.wireOp",EDGE,"E1.sketch_text.stroke-23")])],"isStart":false})],"blendedInto":[]});
            var Q61;
            Q61=makeQuery(id+"F2.opFillet","BLEND_EDGE",EDGE,{"blendedFrom":[makeQuery(id+"F1.opExtrude","CAP_EDGE",EDGE,{"disambiguationData":[OSD([sQuery(id+"F0.wireOp",EDGE,"E1.sketch_text.stroke-33")])],"isStart":false}),makeQuery(id+"F1.opExtrude","CAP_EDGE",EDGE,{"disambiguationData":[OSD([sQuery(id+"F0.wireOp",EDGE,"E1.sketch_text.stroke-34")])],"isStart":false})],"blendedInto":[]});
            var Q62;
            Q62=makeQuery(id+"F2.opFillet","BLEND_EDGE",EDGE,{"blendedFrom":[makeQuery(id+"F1.opExtrude","CAP_EDGE",EDGE,{"disambiguationData":[OSD([sQuery(id+"F0.wireOp",EDGE,"E1.sketch_text.stroke-35")])],"isStart":false}),makeQuery(id+"F1.opExtrude","CAP_EDGE",EDGE,{"disambiguationData":[OSD([sQuery(id+"F0.wireOp",EDGE,"E1.sketch_text.stroke-36")])],"isStart":false})],"blendedInto":[]});
            var Q63;
            Q63=makeQuery(id+"F2.opFillet","BLEND_EDGE",EDGE,{"blendedFrom":[makeQuery(id+"F1.opExtrude","CAP_EDGE",EDGE,{"disambiguationData":[OSD([sQuery(id+"F0.wireOp",EDGE,"E0.sketch_text.stroke-10")])],"isStart":false}),makeQuery(id+"F1.opExtrude","CAP_EDGE",EDGE,{"disambiguationData":[OSD([sQuery(id+"F0.wireOp",EDGE,"E0.sketch_text.stroke-11")])],"isStart":false})],"blendedInto":[]});
            var Q64;
            Q64=makeQuery(id+"F2.opFillet","BLEND_EDGE",EDGE,{"blendedFrom":[makeQuery(id+"F1.opExtrude","CAP_EDGE",EDGE,{"disambiguationData":[OSD([sQuery(id+"F0.wireOp",EDGE,"E0.sketch_text.stroke-13")])],"isStart":false}),makeQuery(id+"F1.opExtrude","CAP_EDGE",EDGE,{"disambiguationData":[OSD([sQuery(id+"F0.wireOp",EDGE,"E0.sketch_text.stroke-14")])],"isStart":false})],"blendedInto":[]});
            var Q65;
            Q65=makeQuery(id+"F2.opFillet","BLEND_EDGE",EDGE,{"blendedFrom":[makeQuery(id+"F1.opExtrude","CAP_EDGE",EDGE,{"disambiguationData":[OSD([sQuery(id+"F0.wireOp",EDGE,"E0.sketch_text.stroke-30")])],"isStart":false}),makeQuery(id+"F1.opExtrude","CAP_EDGE",EDGE,{"disambiguationData":[OSD([sQuery(id+"F0.wireOp",EDGE,"E0.sketch_text.stroke-31")])],"isStart":false})],"blendedInto":[]});
            fillet(context, id + "F3", {"entities" : qUnion([Q0, Q1, Q2, Q3, Q4, Q5, Q6, Q7, Q8, Q9, Q10, Q11, Q12, Q13, Q14, Q15, Q16, Q17, Q18, Q19, Q20, Q21, Q22, Q23, Q24, Q25, Q26, Q27, Q28, Q29, Q30, Q31, Q32, Q33, Q34, Q35, Q36, Q37, Q38, Q39, Q40, Q41, Q42, Q43, Q44, Q45, Q46, Q47, Q48, Q49, Q50, Q51, Q52, Q53, Q54, Q55, Q56, Q57, Q58, Q59, Q60, Q61, Q62, Q63, Q64, Q65]), "radius" : 1.27 * mm, "tangentPropagation" : true, "allowEdgeOverflow" : false});
        }
    });
